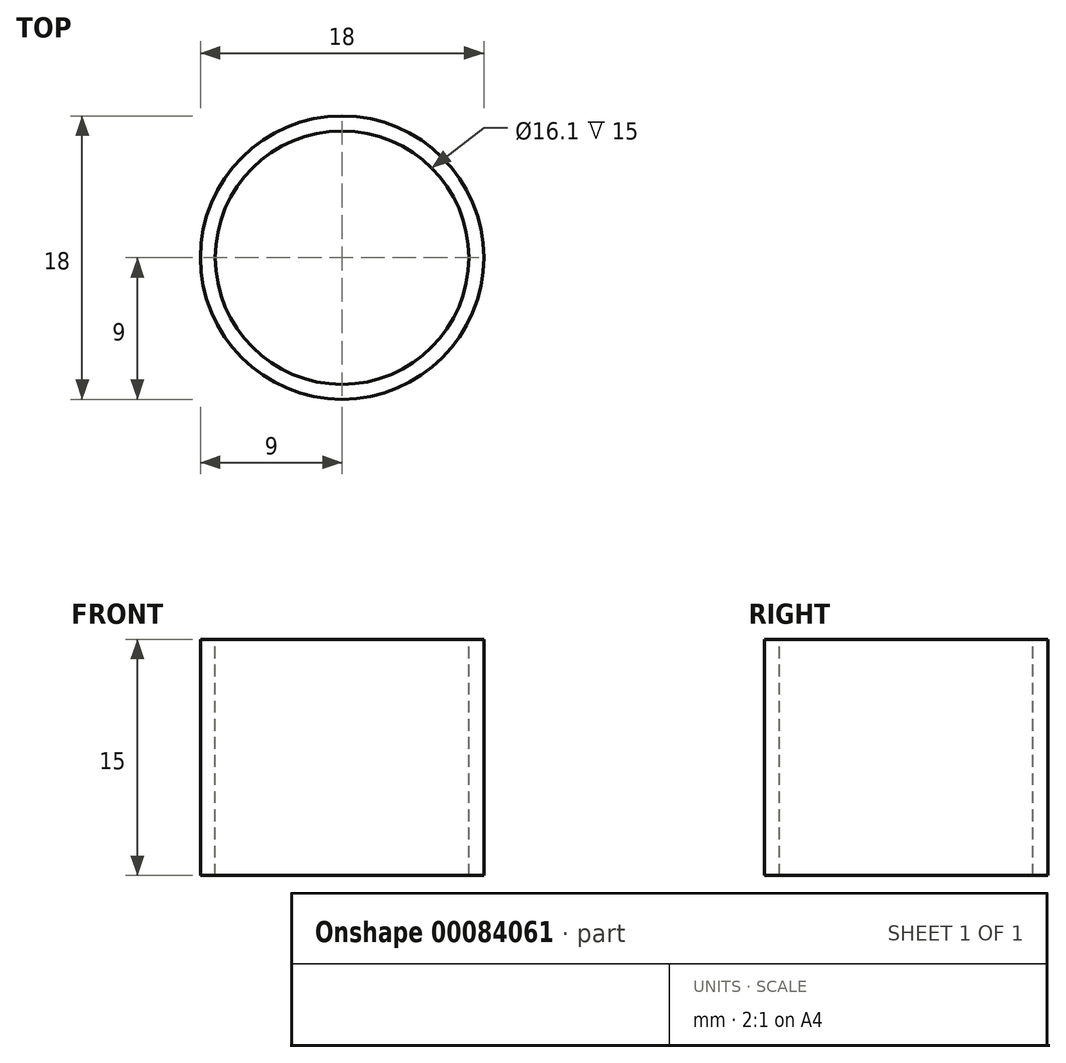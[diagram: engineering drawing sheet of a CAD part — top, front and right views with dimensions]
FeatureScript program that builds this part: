
annotation { "Feature Type Name" : "Feature", "Feature Type Description" : "" }
export const myFeature = defineFeature(function(context is Context, id is Id, definition is map)
    precondition{}
    {
        {
            var Q0;
            Q0=qCreatedBy(makeId("Top.planeOp"),FACE);
            var sketch = newSketch(context, id + "F0", { "sketchPlane" : qUnion([Q0])});
            skCircle(sketch, "E0", {"center": v(0, 0) * mm, "radius": 8.05 * mm});
            skCircle(sketch, "E1", {"center": v(0, 0) * mm, "radius": 9 * mm});
            skSolve(sketch);
        }
        {
            var Q0;
            Q0=makeQuery(id+"F0.imprint","IMPRINT",FACE,{"disambiguationData":[TD([[makeQuery(id+"F0.imprint","IMPRINT",EDGE,{"derivedFrom":sQuery(id+"F0.wireOp",EDGE,"E0")}),-1.0]])]});
            extrude(context, id + "F1", {"entities" : qUnion([Q0]), "oppositeDirection" : true, "depth" : 15 * mm});
        }
    });
